# Revit family: 32_Berkvens_Verdi 202 WD100_v1.3
name_source: partatom
category: Doors
units: mm (PartAtom-declared; Revit-internal decimal feet)

## family parameters
Always vertical = Yes
Cut with Voids When Loaded = No
Host = Wall
OmniClass Number = 23.30.10.00
OmniClass Title = Doors
Room Calculation Point = Yes
Shared = No

## types (7) — shared parameters
60_45 Model kozijn = RZ dubbeldeurs
60_63 Vloerplafondhoogte = 2610 mm  [stored 8.56299 ft]
60_81 Uitvoering kozijn = Kozijn zonder bovenlicht
60_84 Type kozijn = Verdi stalen montagekozijn
70_88 Uitvoering deur = standaard
70_90 Type deur = Berklon, lakdeur
80_30 Krukgathoogte = 1050 mm
80_60 Kantuitvoering = opdek
80_75 Deurhoogte = 2500 mm  [stored 8.2021 ft]
Analytic Construction = <None>
Assembly Code = 2E(32.31)
Compartmentation = No
FireExit = No
Function = Interior
IsExternal = No
M1 = Berkvens_kristalwit
M2 = Berkvens_kristalwit
M3 = Berkvens_kristalwit
M4 = Berkvens_kristalwit
M5 = Berkvens_kristalwit
M6 = Berkvens_kristalwit
Manufacturer = Berkvens
Model = Verdi
SelfClosing = No
SmokeStop = No
URL = www.berkvens.nl
Versie = 1.3
Wall Closure = By host
zero-valued in all types: Height, Width

## per-type parameters (varying)
| type | 80_85 Deurbreedte passieve deur | 80_90 Deurbreedte actieve deur |
| 930(x2) x VL-PL hoogte | 930 mm  [stored 3.05118 ft] | 930 mm  [stored 3.05118 ft] |
| 730(x2) x VL-PL hoogte | 730 mm  [stored 2.39501 ft] | 730 mm  [stored 2.39501 ft] |
| 780(x2) x VL-PL hoogte | 780 mm  [stored 2.55906 ft] | 780 mm  [stored 2.55906 ft] |
| 830(x2) x VL-PL hoogte | 830 mm  [stored 2.7231 ft] | 830 mm  [stored 2.7231 ft] |
| 880(x2) x VL-PL hoogte | 880 mm  [stored 2.88714 ft] | 880 mm  [stored 2.88714 ft] |
| 980(x2) x VL-PL hoogte (980 = meerprijs) | 980 mm  [stored 3.21522 ft] | 980 mm  [stored 3.21522 ft] |
| 1030(x2) x VL-PL hoogte (1030 = meerprijs) | 1030 mm  [stored 3.37927 ft] | 1030 mm  [stored 3.37927 ft] |

note: [stored X ft] marks values corroborated as IEEE doubles in the binary element streams (Revit-internal decimal feet)

## geometry (parser evidence)
native form markers: Sweep x45
no freeform markers — native parametric forms only
